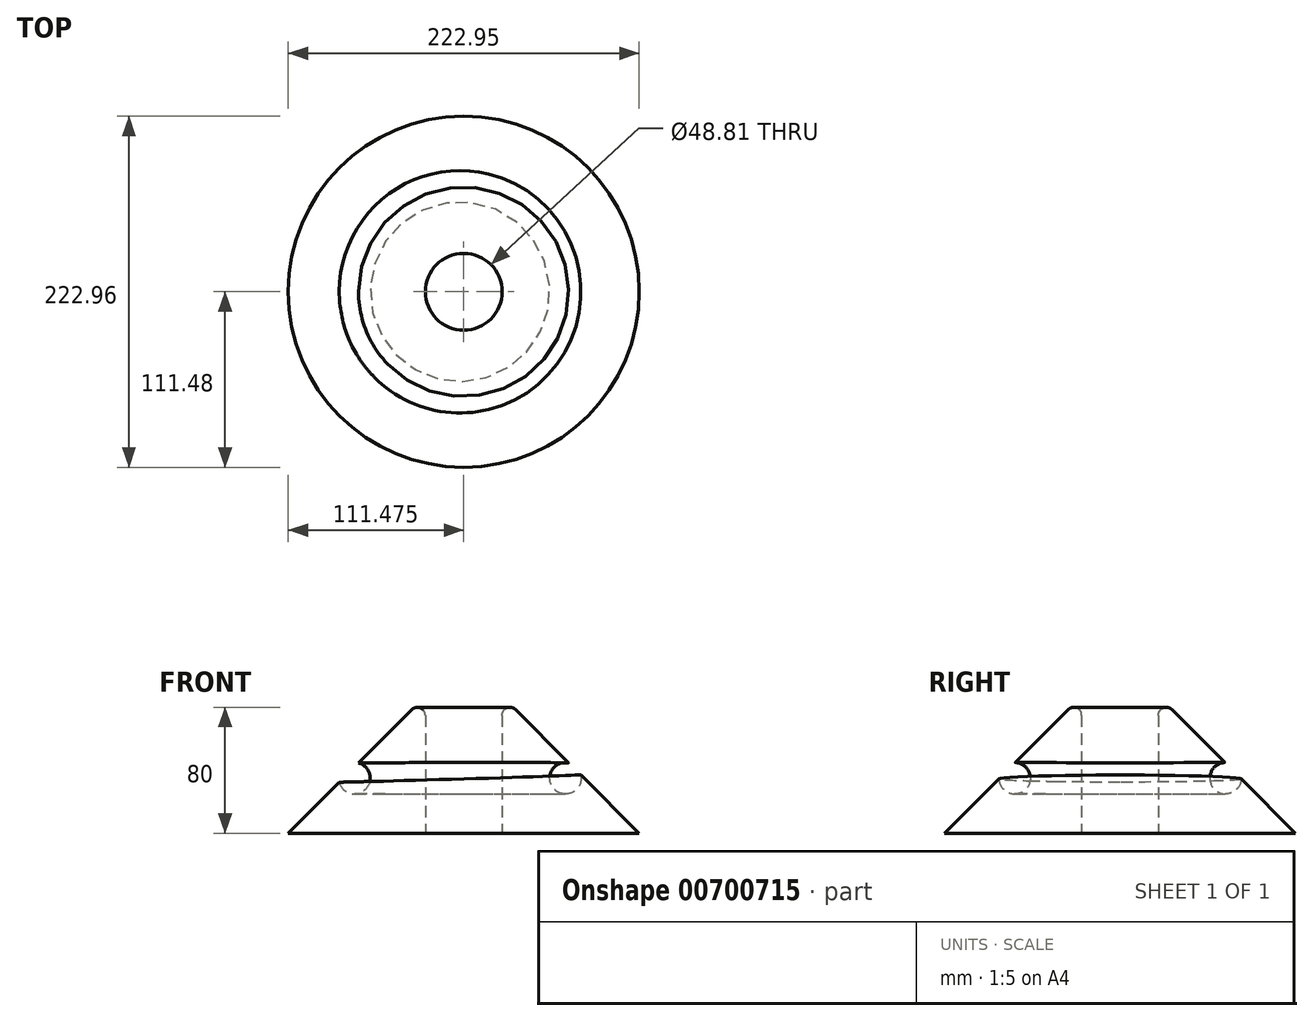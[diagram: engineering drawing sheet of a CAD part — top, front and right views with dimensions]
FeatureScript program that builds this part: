
annotation { "Feature Type Name" : "Feature", "Feature Type Description" : "" }
export const myFeature = defineFeature(function(context is Context, id is Id, definition is map)
    precondition{}
    {
        {
            var Q0;
            Q0=qCreatedBy(makeId("Front.planeOp"),FACE);
            var sketch = newSketch(context, id + "F0", { "sketchPlane" : qUnion([Q0])});
            skLineSegment(sketch, "E0", {"start": v(-87.07, 0) * mm, "end": v(-8.54, 78.54) * mm});
            skLineSegment(sketch, "E1", {"start": v(0, 75) * mm, "end": v(0, 0) * mm});
            skLineSegment(sketch, "E2", {"start": v(0, 0) * mm, "end": v(-87.07, 0) * mm});
            skPoint(sketch, "E3.visualSharp", {"position": v(0, 87.07) * mm});
            skArc(sketch, "E3.filletArc", {"start": v(0, 75) * mm, "mid": v(-3.09, 79.62) * mm, "end": v(-8.54, 78.54) * mm});
            skLineSegment(sketch, "E4", {"start": v(24.4, 0) * mm, "end": v(24.4, 81.33) * mm, "construction": true});
            skPoint(sketch, "E4.startSnap0", {"position": v(-43.54, 0) * mm});
            skSolve(sketch);
        }
        {
            var Q0;
            Q0=makeQuery(id+"F0.imprint","IMPRINT",FACE,{"disambiguationData":[TD([[makeQuery(id+"F0.imprint","IMPRINT",EDGE,{"derivedFrom":sQuery(id+"F0.wireOp",EDGE,"E0")}),-1.0]])]});
            var Q1;
            Q1=sQuery(id+"F0.wireOp",EDGE,"E4");
            revolve(context, id + "F1", {"entities" : qUnion([Q0]), "axis" : qUnion([Q1]), "revolveType" : RevolveType.FULL});
        }
        {
            var Q0;
            Q0=qCreatedBy(makeId("Front.planeOp"),FACE);
            var sketch = newSketch(context, id + "F2", { "sketchPlane" : qUnion([Q0])});
            skCircle(sketch, "E5", {"center": v(-45, 35) * mm, "radius": 10 * mm});
            skLineSegment(sketch, "E6", {"start": v(22, 0) * mm, "end": v(22, 105.32) * mm, "construction": true});
            skSolve(sketch);
        }
        {
            var Q0;
            Q0=makeQuery(id+"F2.imprint","IMPRINT",FACE,{"disambiguationData":[TD([[makeQuery(id+"F2.imprint","IMPRINT",EDGE,{"derivedFrom":sQuery(id+"F2.wireOp",EDGE,"E5")}),1.0]])]});
            var Q1;
            Q1=sQuery(id+"F2.wireOp",EDGE,"E6");
            revolve(context, id + "F3", {"operationType" : NewBodyOperationType.REMOVE, "entities" : qUnion([Q0]), "axis" : qUnion([Q1]), "revolveType" : RevolveType.FULL, "oppositeDirection" : true});
        }
    });
